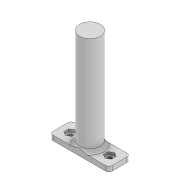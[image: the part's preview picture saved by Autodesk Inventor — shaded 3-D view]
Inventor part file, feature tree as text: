
AUTODESK INVENTOR PART (.ipt)
format: ipt  version: 2020 (Build 240168000, 168)  size: 164,864 bytes
history: native  units: mm
features: extrude x4, sketch x4, fillet x2
ambient origin geometry x8: Origin, YZ Plane, XZ Plane, XY Plane, X Axis, Y Axis, Z Axis, Center Point
bodies: Solid1 (feature_tree)
feature tree (10):
  extrude  "Extrusion1"  Depth=60.0mm TaperAngle=0.0deg
  extrude  "Extrusion2"  Depth=12.0mm
  fillet  "Fillet1"  Radius=36.0mm
  fillet  "Fillet2"  Radius=13.0mm
  extrude  "Extrusion3"  Depth=2.0mm
  extrude  "Extrusion4"  Depth=5.0mm
  sketch  "Sketch1"  dims[d0=12.6mm d1=60.0mm d2=0.0mm]
  sketch  "Sketch2"  dims[d3=2.7mm d4=12.0mm d5=36.0mm d6=13.0mm]
  sketch  "Sketch3"  dims[d7=3.0mm d8=0.0mm d9=2.0mm]
  sketch  "Sketch4"  dims[d10=2.0mm d11=5.0mm d12=5.0mm d13=1.5mm d14=0.0mm d15=5.0mm d16=5.0mm d17=4.0mm d18=3.5mm d19=4.0mm d20=3.5mm d21=2.0mm d22=0.0mm]
